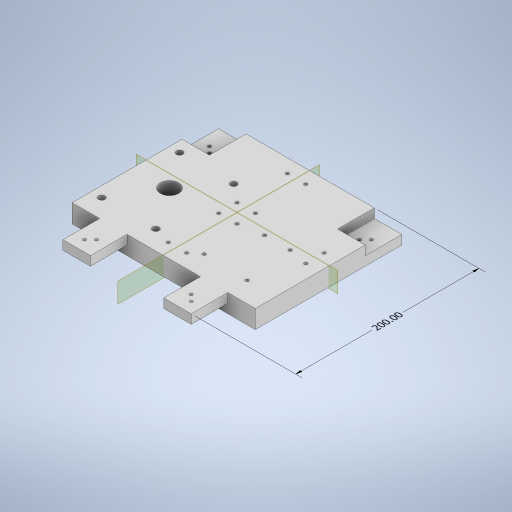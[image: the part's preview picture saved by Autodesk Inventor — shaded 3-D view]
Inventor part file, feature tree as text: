
AUTODESK INVENTOR PART (.ipt)
format: ipt  version: 2023 (Build 270158000, 158)  size: 432,128 bytes
history: native  units: mm
features: sketch x10, extrude x5, hole x5, other x3, plane x2
ambient origin geometry x8: Origin, YZ Plane, XZ Plane, XY Plane, X Axis, Y Axis, Z Axis, Center Point
bodies: Body1 (feature_tree)
feature tree (25):
  other  "Sólido1"
  other  "Anotaciones"
  extrude  "Extrusión1"  Depth=160.0mm
  extrude  "Extrusión2"  Depth=30.0mm
  hole  "Agujero1"  [1 undecoded]
  extrude  "Extrusión3"  Depth=11.75mm
  hole  "Agujero2"  [1 undecoded]
  hole  "Agujero3"  [1 undecoded]
  extrude  "Extrusión4"  TaperAngle=0.0deg  [1 undecoded]
  plane  "Plano de trabajo1"
  plane  "Plano de trabajo2"
  hole  "Agujero4"  [1 undecoded]
  hole  "Agujero5"  [1 undecoded]
  extrude  "Extrusión5"  Depth=200.0mm
  sketch  "Boceto1"  dims[d0=200.0mm d1=160.0mm]
  sketch  "Boceto2"  dims[d2=20.0mm d3=0.0mm d4=30.0mm]
  sketch  "Boceto3"  dims[d5=40.0mm d6=10.0mm d7=0.0mm]
  sketch  "Boceto4"  dims[d23=21.75mm d24=11.75mm]
  sketch  "Boceto5"  dims[d26=11.75mm]
  sketch  "Boceto6"  dims[d27=3.5mm d28=6.0mm d29=4.0mm d30=2.0mm d31=90.0deg d32=8.0mm d33=20.594885mm d34=30.0mm]
  sketch  "Boceto7"  dims[d35=10.0mm d36=30.0mm]
  sketch  "Boceto8"  dims[d37=40.0mm d38=0.0mm]
  sketch  "Boceto9"  dims[d39=10.0mm d40=10.0mm d41=40.0mm d42=0.0mm d43=6.5mm d44=6.5mm d45=3.5mm d46=3.5mm d47=11.749873mm d48=11.75mm d49=0.0mm]
  sketch  "Boceto10"  dims[d50=11.75mm d51=0.0mm d52=3.5mm d53=6.0mm d54=4.0mm d55=2.0mm d56=90.0deg d57=8.0mm d58=20.594885mm d59=7.0mm d60=7.0mm d61=7.0mm d62=39.0mm d63=46.0mm d64=59.0mm d65=46.0mm d66=39.0mm d67=59.0mm d68=52.0mm d69=70.0mm d70=22.0mm d71=42.0mm d72=3.5mm d73=3.5mm d74=3.5mm d75=3.5mm d76=3.5mm d77=6.0mm d78=4.0mm d79=2.0mm d80=90.0deg d81=8.0mm d82=20.594885mm d83=7.0mm d84=7.0mm d85=7.0mm d86=39.0mm d87=46.0mm d88=59.0mm d89=46.0mm d90=39.0mm d91=59.0mm d92=20.0mm d93=0.0mm d97=40.000127mm d98=10.0mm d99=30.0mm d100=10.0mm d101=5.0mm d102=5.0mm d103=5.0mm d104=5.0mm d105=45.0deg d106=45.0deg d107=10.0mm d108=10.0mm d109=30.0mm d110=5.0mm d111=5.0mm d112=5.0mm d113=5.0mm d114=10.0mm d115=30.0mm d116=5.0mm d117=5.0mm d118=5.0mm d119=5.0mm d120=10.0mm d121=3.5mm d122=6.0mm d123=4.0mm d124=2.0mm d125=90.0deg d126=8.0mm d127=20.594885mm d128=3.5mm d129=10.0mm d130=10.0mm d131=3.5mm d132=6.0mm d133=4.0mm d134=2.0mm d135=90.0deg d136=8.0mm d137=20.594885mm d138=32.0mm d139=32.0mm d140=10.0mm d141=0.0mm d142=17.37633mm d143=12.709242mm d144=6.683722mm d145=12.708891mm d146=5.220756mm d147=1.603663mm d148=2.153068mm d149=6.490327mm d94=6.100674mm d95=2.550465mm d96=200.0mm]
  other  "Cota lineal 1"
note: 6 required parameter values undecoded (feature->parameter linkage not recoverable at this tier; creation-order binding heuristic only, values carry confidence <= 0.55)
